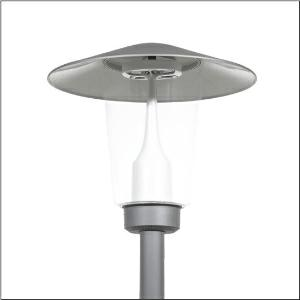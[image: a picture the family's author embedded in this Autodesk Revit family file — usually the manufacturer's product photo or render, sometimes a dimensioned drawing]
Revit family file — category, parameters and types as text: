
# Revit family: pilzleuchte_iq___st1_2a_5xa5235kf14h_dd17
name_source: partatom
category: Lighting Fixtures
units: mm (PartAtom-declared; Revit-internal decimal feet)

## family parameters
Cut with Voids When Loaded = No
Host = Face
Light Source = No
Part Type = Normal
Room Calculation Point = No
Round Connector Dimension = Use Diameter
Shared = No

## types (1)
- --- (1 x LED, 1550 lm, 10 W, 4000K)
    Apparent Load = 10 VA
    CIE Flux Codes = 24 61 93 98 100
    Color Rendering = 70
    Color Temperature = 4000K
    Default Elevation = 1800 mm
    Description = Mushroom Luminaire iQ, mast luminaire, Module 540 iQ-SR, primary light control with 3 zone facetted reflector, of plastic, silver coated, highly specular, structured, primary optical cover: cover, of PMMA, transparent, light distribution: ST1.2a, light emission: direct distribution, primary light characteristic: asymmetric, installation type: post-top, LED, High Power LED, rated luminous flux: 1.550lm, luminous efficacy: 155lm/W, light colour: 740, colour temperature: 4000K, control gear: ECG iQ, control: presetting dimming logarithmic, Street-Remote, Auto-Match, Temp-Guard, Lumen-Switch, Night-Set, Smart-Wire, Light-Fading, Desk-Remote (wireless, voltage-free reading and setting of iQ features in the workshop via application-optimized NFC function/RFID function), optimised constant luminous flux control (CLO 2.0), with terminal, 6-pole, max. 2.5mm², mains connection: 230..240V, AC, 50/60Hz, start of lifetime: 10W, end of service life: 10W, reduction: 5W, luminaire housing, upper part, of glass-fibre reinforced polyester, coated, Siteco® metallic grey (DB 702S), diameter: 650mm, height: 586mm, spigot size: d x l = 76 x 70mm (post-top) | with reducer (optional accessory) 60 x 70mm, post-top mast mounting element, of diecast aluminium, coated, Siteco® metallic grey (DB 702S), Module 540 iQ-SR, traffic white (RAL 9016), equipment: standard, protection rating (complete): IP65, insulation class (complete): insulation class II (safety insulation), certification: CE, ENEC, VDE, packaging unit: 1 piece

Light Distribution: ST1.2a
    Height = 586 mm
    Lamp = 1 x LED
    Lamp Light Flux = 1550 lm
    Lamp Power = 10 W
    Lamp count = 1
    Length = 650 mm
    Luminous efficacy = 155 lm/W
    Manufacturer = Siteco
    ModVariant = No
    Model = 5XA5235KF14H
    Number of Poles = 1
    OnlyDefault = Yes
    Power Factor = 1
    Product Name = Pilzleuchte iQ | ST1.2a
    Product group = mast luminaire | pylon top
    ProductGroupID = 6100
    Protection Class = Protection class II
    Protection Degree = IP 65
    RLX_Detail_Level = 1
    RLX_Emergency_Light_Flux = 0 lm
    RLX_Emergency_Type = 0
    RLX_Emergency_Type_DB = No
    RlxData = <blob elided: 126945 chars, md5=c9191bc0>
    Socket = socket
    Standby Power = 0 W
    System Light Flux = 1550 lm
    System Power = 10 W
    Type Comments = factory setting: luminous flux: 100 % | dim-lin: 254 | 401 mA
    Type Image = l_1006077.jpg
    URL = http://relux.com
    VarID = @adj_093057
    Voltage = 0 V
    Weight = 0.00 kg
    Width = 0 mm  [stored 0 ft]

note: [stored X ft] marks values corroborated as IEEE doubles in the binary element streams (Revit-internal decimal feet)

## geometry (parser evidence)
native form markers: Blend x4, Sweep x12
no freeform markers — native parametric forms only
